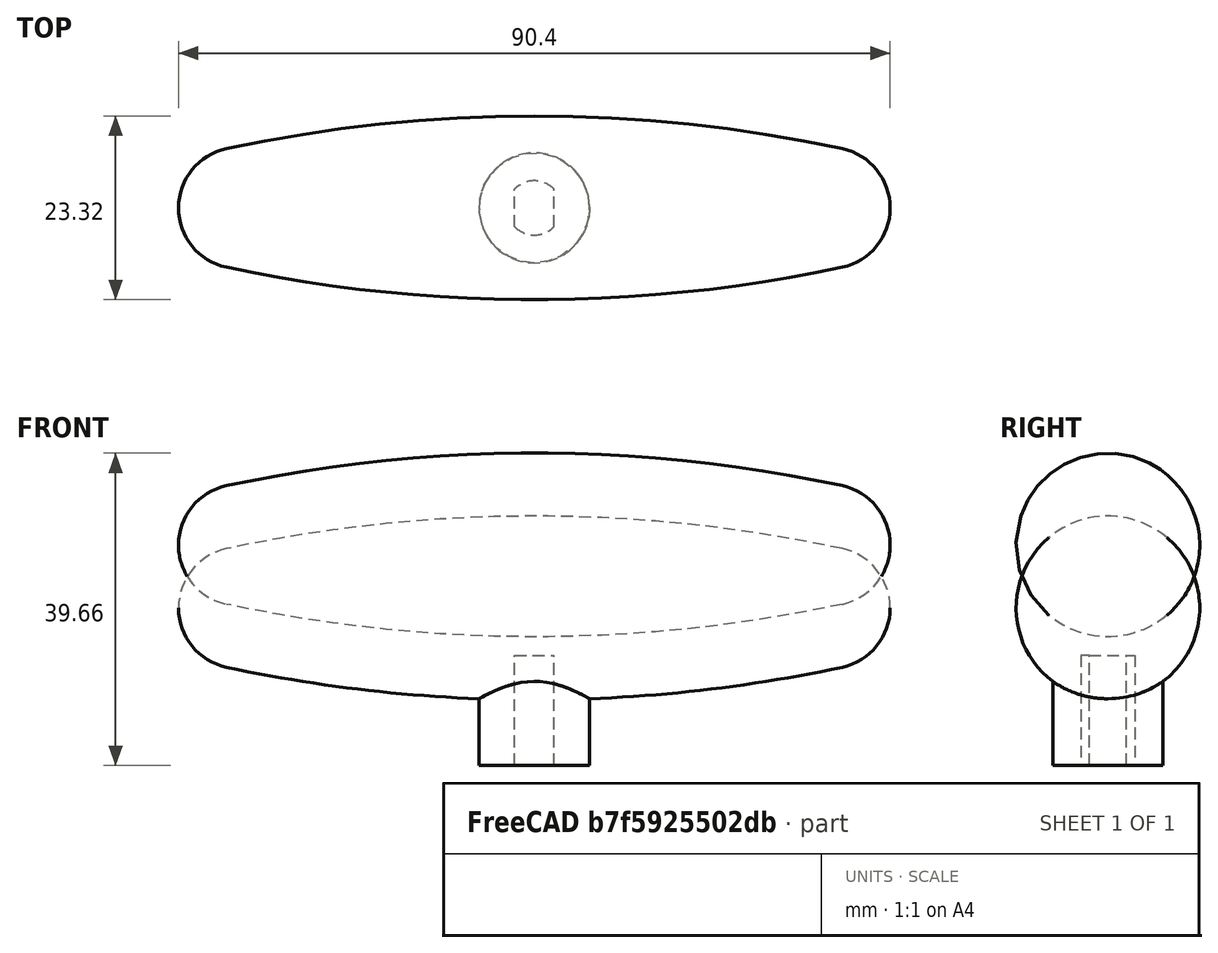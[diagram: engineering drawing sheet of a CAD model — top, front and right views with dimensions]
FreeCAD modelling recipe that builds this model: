
FCSTD DOCUMENT  (FreeCAD 0.19R23756 (Git))
Label: abort_handle_v3
License: All rights reserved
LicenseURL: http://en.wikipedia.org/wiki/All_rights_reserved
objects: Sketcher::SketchObject×3, PartDesign::Body×2, PartDesign::Revolution×1, PartDesign::Pad×1, PartDesign::Boolean×1, PartDesign::Pocket×1, Mesh::Feature×1
note: 12 computed .brp shape members not serialized (recipe doc carries the construction recipe); baked Part::Feature solids carry a one-line shape summary decoded from their .brp

FEATURE [Sketcher::SketchObject] Sketch
  FullyConstrained = true
  MapMode = 5
  Support = -> [XY_Plane]
  sketch-geometry (4):
    g0: ArcOfCircle CenterX=-37.5 CenterY=5e-16 CenterZ=0 NormalX=0 NormalY=0 NormalZ=1 AngleXU=0 Radius=7.69885 StartAngle=1.78147 EndAngle=3.14159
    g1: ArcOfCircle CenterX=-1.68e-14 CenterY=-175.356 CenterZ=0 NormalX=0 NormalY=0 NormalZ=1 AngleXU=0 Radius=187.02 StartAngle=1.36012 EndAngle=1.78147
    g2: ArcOfCircle CenterX=37.5 CenterY=5e-16 CenterZ=0 NormalX=0 NormalY=0 NormalZ=1 AngleXU=0 Radius=7.69885 StartAngle=0 EndAngle=1.36012
    g3: LineSegment StartX=-45.1989 StartY=0 StartZ=0 EndX=45.1989 EndY=0 EndZ=0
  constraints (13):
    c: Coincident(g2,g1)
    c: Horizontal(g0,g1)
    c: Horizontal(g2,g0)
    c: Tangent(g2,g1,g1) = -1.5708
    c: Tangent(g1,g0) = -1.5708
    c: DistanceX(g0,g2) = 75
    c: Coincident(g3,g0)
    c: Coincident(g3,g2)
    c: Horizontal(g3)
    c: Angle(g0,g3,g0) = 1.5708
    c: Symmetric(g2,g0,g-1)
    c: DistanceX(g0,g1) = 78.22
    c: Radius(g1) = 187.02
FEATURE [PartDesign::Revolution] Revolution
  Angle = 360
  Axis = (1,0,0)
  Base = (0,0,0)
  Profile = -> Sketch
  ReferenceAxis = -> X_Axis
FEATURE [PartDesign::Body] Body
  Group = -> [Sketch,Revolution]
  Origin = -> Origin
  Tip = -> Revolution
FEATURE [Sketcher::SketchObject] Sketch001  label="stem"
  FullyConstrained = true
  MapMode = 5
  Support = -> [XY_Plane001]
  sketch-geometry (1):
    g0: Circle CenterX=0 CenterY=0 CenterZ=0 NormalX=0 NormalY=0 NormalZ=1 AngleXU=0 Radius=7
  constraints (2):
    c: Coincident(g0,g-1)
    c: Radius(g0) = 7
FEATURE [PartDesign::Pad] Pad
  Direction = (1,1,1)
  Length = 20
  Length2 = 100
  Profile = -> Sketch001
  Reversed = true
  Type = 0
FEATURE [PartDesign::Boolean] Boolean
  BaseFeature = -> Pad
  Group = -> [Body]
  Type = 0
FEATURE [Sketcher::SketchObject] Sketch002  label="hole"
  FullyConstrained = true
  MapMode = 5
  Placement = pos=(0,0,-20) rot=(1,0,0;3.14159rad)
  Support = -> [Boolean]
  sketch-geometry (4):
    g0: ArcOfCircle CenterX=0 CenterY=0 CenterZ=0 NormalX=0 NormalY=0 NormalZ=1 AngleXU=0 Radius=3.45 StartAngle=0.760288 EndAngle=2.3813
    g1: ArcOfCircle CenterX=0 CenterY=0 CenterZ=0 NormalX=0 NormalY=0 NormalZ=1 AngleXU=0 Radius=3.45 StartAngle=3.90188 EndAngle=5.5229
    g2: LineSegment StartX=-2.5 StartY=2.3775 StartZ=0 EndX=-2.5 EndY=-2.3775 EndZ=0
    g3: LineSegment StartX=2.5 StartY=2.3775 StartZ=0 EndX=2.5 EndY=-2.3775 EndZ=0
  constraints (12):
    c: Coincident(g2,g0)
    c: Coincident(g2,g1)
    c: Coincident(g3,g0)
    c: Coincident(g3,g1)
    c: Vertical(g2)
    c: Vertical(g3)
    c: Coincident(g0,g1)
    c: Horizontal(g0,g0)
    c: DistanceX(g0,g0) = 5  'stem width'
    c: Equal(g1,g0)
    c: Coincident(g0,g-1)
    c: Radius(g0) = 3.45
FEATURE [PartDesign::Pocket] Pocket
  BaseFeature = -> Boolean
  Length = 14
  Length2 = 100
  Profile = -> Sketch002
  Type = 0
FEATURE [PartDesign::Body] Body001
  Group = -> [Sketch001,Pad,Boolean,Sketch002,Pocket]
  Origin = -> Origin001
  Placement = pos=(0,0,-8) rot=(0,0,1;0rad)
  Tip = -> Pocket
FEATURE [Mesh::Feature] Mesh001  label="mephisto_mesh_v2"
